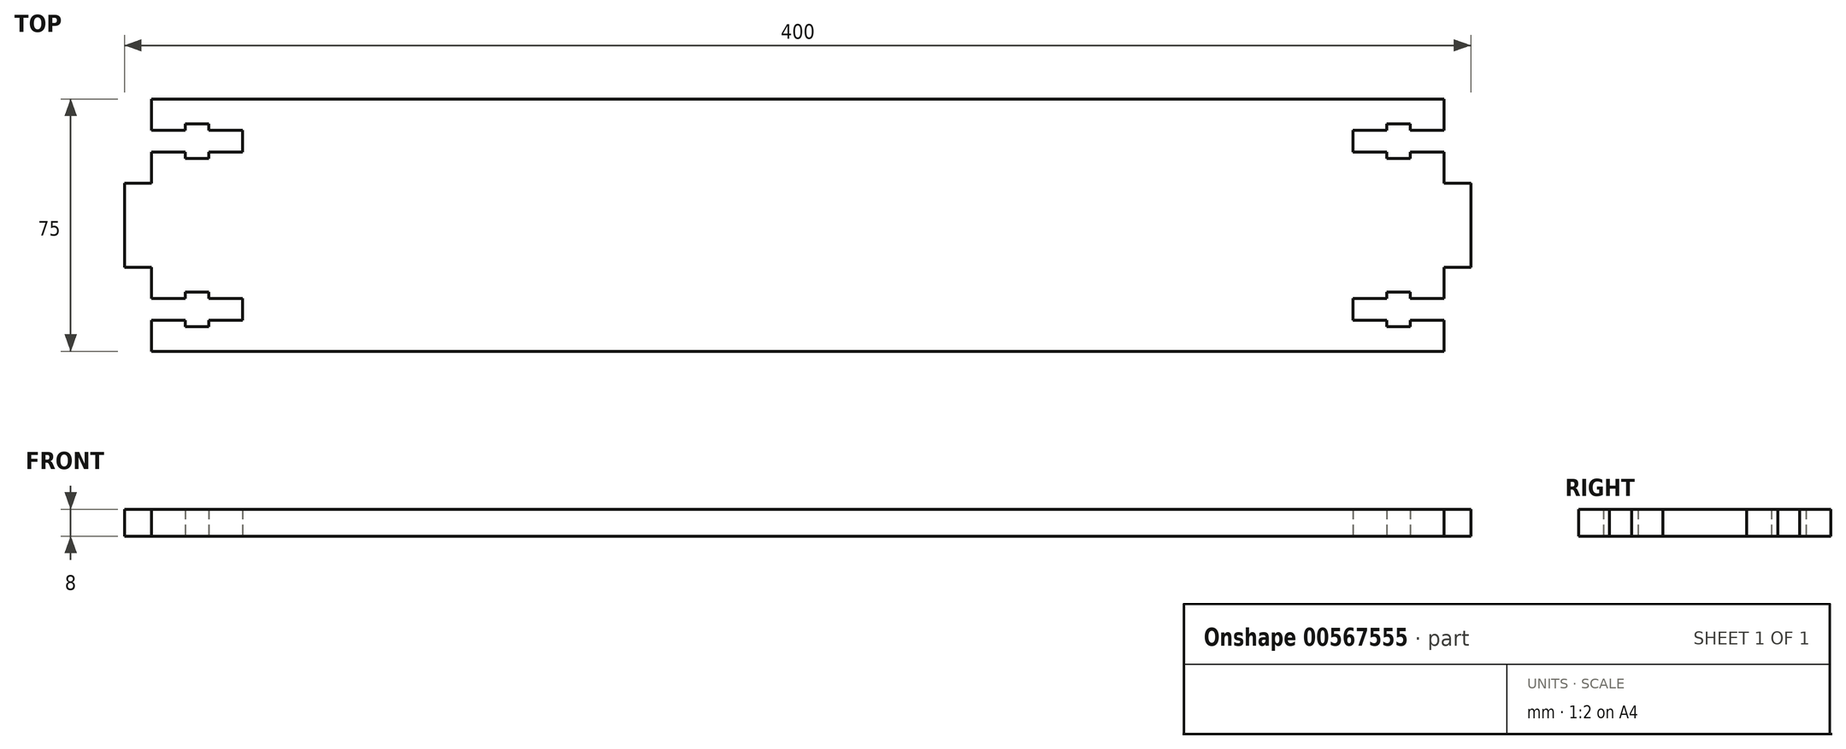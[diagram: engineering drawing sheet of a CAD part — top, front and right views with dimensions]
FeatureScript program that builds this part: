
annotation { "Feature Type Name" : "Feature", "Feature Type Description" : "" }
export const myFeature = defineFeature(function(context is Context, id is Id, definition is map)
    precondition{}
    {
        {
            var Q0;
            Q0=qCreatedBy(makeId("Top.planeOp"),FACE);
            var sketch = newSketch(context, id + "F0", { "sketchPlane" : qUnion([Q0])});
            skLineSegment(sketch, "E0", {"start": v(0, 0) * mm, "end": v(0, 9.25) * mm});
            skLineSegment(sketch, "E1", {"start": v(0, 25) * mm, "end": v(-8, 25) * mm});
            skLineSegment(sketch, "E2", {"start": v(-8, 25) * mm, "end": v(-8, 50) * mm});
            skLineSegment(sketch, "E3", {"start": v(-8, 50) * mm, "end": v(0, 50) * mm});
            skLineSegment(sketch, "E4", {"start": v(0, 75) * mm, "end": v(384, 75) * mm});
            skLineSegment(sketch, "E5", {"start": v(384, 0) * mm, "end": v(0, 0) * mm});
            skLineSegment(sketch, "E6", {"start": v(384, 75) * mm, "end": v(384, 65.75) * mm});
            skLineSegment(sketch, "E7", {"start": v(384, 50) * mm, "end": v(392, 50) * mm});
            skLineSegment(sketch, "E8", {"start": v(392, 50) * mm, "end": v(392, 25) * mm});
            skLineSegment(sketch, "E9", {"start": v(392, 25) * mm, "end": v(384, 25) * mm});
            skLineSegment(sketch, "E10", {"start": v(384, 25) * mm, "end": v(384, 15.75) * mm});
            skLineSegment(sketch, "E11", {"start": v(0, 65.75) * mm, "end": v(10, 65.75) * mm});
            skLineSegment(sketch, "E12", {"start": v(10, 65.75) * mm, "end": v(10, 67.65) * mm});
            skLineSegment(sketch, "E13", {"start": v(10, 67.65) * mm, "end": v(17, 67.65) * mm});
            skLineSegment(sketch, "E14", {"start": v(17, 67.65) * mm, "end": v(17, 65.75) * mm});
            skLineSegment(sketch, "E15", {"start": v(17, 65.75) * mm, "end": v(27, 65.75) * mm});
            skLineSegment(sketch, "E16", {"start": v(27, 65.75) * mm, "end": v(27, 59.25) * mm});
            skLineSegment(sketch, "E17", {"start": v(27, 59.25) * mm, "end": v(17, 59.25) * mm});
            skLineSegment(sketch, "E18", {"start": v(17, 59.25) * mm, "end": v(17, 57.35) * mm});
            skLineSegment(sketch, "E19", {"start": v(17, 57.35) * mm, "end": v(10, 57.35) * mm});
            skLineSegment(sketch, "E20", {"start": v(10, 57.35) * mm, "end": v(10, 59.25) * mm});
            skLineSegment(sketch, "E21", {"start": v(10, 59.25) * mm, "end": v(0, 59.25) * mm});
            skPoint(sketch, "E22", {"position": v(27, 62.5) * mm});
            skLineSegment(sketch, "E23", {"start": v(0, 65.75) * mm, "end": v(0, 75) * mm});
            skLineSegment(sketch, "E24", {"start": v(0, 50) * mm, "end": v(0, 59.25) * mm});
            skLineSegment(sketch, "E25", {"start": v(-8, 37.5) * mm, "end": v(45.1, 37.5) * mm, "construction": true});
            skPoint(sketch, "E25.endSnap0", {"position": v(-8, 37.5) * mm});
            skLineSegment(sketch, "E26", {"start": v(192, 75) * mm, "end": v(192, 49.53) * mm, "construction": true});
            skLineSegment(sketch, "E27.MirrorCS", {"start": v(10, 15.75) * mm, "end": v(0, 15.75) * mm});
            skLineSegment(sketch, "E28.MirrorCS", {"start": v(10, 17.65) * mm, "end": v(10, 15.75) * mm});
            skLineSegment(sketch, "E29.MirrorCS", {"start": v(17, 17.65) * mm, "end": v(10, 17.65) * mm});
            skLineSegment(sketch, "E30.MirrorCS", {"start": v(17, 15.75) * mm, "end": v(17, 17.65) * mm});
            skLineSegment(sketch, "E31.MirrorCS", {"start": v(27, 15.75) * mm, "end": v(17, 15.75) * mm});
            skLineSegment(sketch, "E32.MirrorCS", {"start": v(27, 9.25) * mm, "end": v(27, 15.75) * mm});
            skLineSegment(sketch, "E33.MirrorCS", {"start": v(17, 9.25) * mm, "end": v(27, 9.25) * mm});
            skLineSegment(sketch, "E34.MirrorCS", {"start": v(17, 7.35) * mm, "end": v(17, 9.25) * mm});
            skLineSegment(sketch, "E35.MirrorCS", {"start": v(10, 7.35) * mm, "end": v(17, 7.35) * mm});
            skLineSegment(sketch, "E36.MirrorCS", {"start": v(10, 9.25) * mm, "end": v(10, 7.35) * mm});
            skLineSegment(sketch, "E37.MirrorCS", {"start": v(0, 9.25) * mm, "end": v(10, 9.25) * mm});
            skLineSegment(sketch, "E38.MirrorCS", {"start": v(367, 7.35) * mm, "end": v(367, 9.25) * mm});
            skLineSegment(sketch, "E39.MirrorCS", {"start": v(367, 15.75) * mm, "end": v(367, 17.65) * mm});
            skLineSegment(sketch, "E40.MirrorCS", {"start": v(374, 17.65) * mm, "end": v(374, 15.75) * mm});
            skLineSegment(sketch, "E41.MirrorCS", {"start": v(374, 9.25) * mm, "end": v(374, 7.35) * mm});
            skLineSegment(sketch, "E42.MirrorCS", {"start": v(374, 7.35) * mm, "end": v(367, 7.35) * mm});
            skLineSegment(sketch, "E43.MirrorCS", {"start": v(357, 9.25) * mm, "end": v(357, 15.75) * mm});
            skLineSegment(sketch, "E44.MirrorCS", {"start": v(357, 15.75) * mm, "end": v(367, 15.75) * mm});
            skLineSegment(sketch, "E45.MirrorCS", {"start": v(367, 17.65) * mm, "end": v(374, 17.65) * mm});
            skLineSegment(sketch, "E46.MirrorCS", {"start": v(367, 9.25) * mm, "end": v(357, 9.25) * mm});
            skLineSegment(sketch, "E47.MirrorCS", {"start": v(384, 9.25) * mm, "end": v(374, 9.25) * mm});
            skLineSegment(sketch, "E48.MirrorCS", {"start": v(374, 15.75) * mm, "end": v(384, 15.75) * mm});
            skLineSegment(sketch, "E49.MirrorCS", {"start": v(374, 59.25) * mm, "end": v(384, 59.25) * mm});
            skLineSegment(sketch, "E50.MirrorCS", {"start": v(367, 57.35) * mm, "end": v(374, 57.35) * mm});
            skLineSegment(sketch, "E51.MirrorCS", {"start": v(374, 67.65) * mm, "end": v(367, 67.65) * mm});
            skLineSegment(sketch, "E52.MirrorCS", {"start": v(367, 67.65) * mm, "end": v(367, 65.75) * mm});
            skLineSegment(sketch, "E53.MirrorCS", {"start": v(367, 65.75) * mm, "end": v(357, 65.75) * mm});
            skLineSegment(sketch, "E54.MirrorCS", {"start": v(384, 65.75) * mm, "end": v(374, 65.75) * mm});
            skLineSegment(sketch, "E55.MirrorCS", {"start": v(374, 65.75) * mm, "end": v(374, 67.65) * mm});
            skPoint(sketch, "E56.MirrorP", {"position": v(357, 62.5) * mm});
            skLineSegment(sketch, "E57.MirrorCS", {"start": v(374, 57.35) * mm, "end": v(374, 59.25) * mm});
            skLineSegment(sketch, "E58.MirrorCS", {"start": v(357, 65.75) * mm, "end": v(357, 59.25) * mm});
            skLineSegment(sketch, "E59.MirrorCS", {"start": v(357, 59.25) * mm, "end": v(367, 59.25) * mm});
            skLineSegment(sketch, "E60.MirrorCS", {"start": v(367, 59.25) * mm, "end": v(367, 57.35) * mm});
            skLineSegment(sketch, "E61.trimOffspring", {"start": v(0, 15.75) * mm, "end": v(0, 25) * mm});
            skLineSegment(sketch, "E62.trimOffspring", {"start": v(384, 59.25) * mm, "end": v(384, 50) * mm});
            skLineSegment(sketch, "E63.trimOffspring", {"start": v(384, 9.25) * mm, "end": v(384, 0) * mm});
            skSolve(sketch);
        }
        {
            var Q0;
            Q0=makeQuery(id+"F0.imprint","IMPRINT",FACE,{"disambiguationData":[TD([[makeQuery(id+"F0.imprint","IMPRINT",EDGE,{"derivedFrom":sQuery(id+"F0.wireOp",EDGE,"E0")}),-1.0]])]});
            extrude(context, id + "F1", {"entities" : qUnion([Q0]), "depth" : 8 * mm, "offsetDistance" : 25 * mm});
        }
    });
